# Revit family: Echo Eliminator - Composite Ceiling and Wall Panels
name_source: partatom
category: Specialty Equipment
units: mm (PartAtom-declared; Revit-internal decimal feet)

## family parameters
Always vertical = No
Cut with Voids When Loaded = No
Enable Cutting in Views = Yes
Maintain Annotation Orientation = No
OmniClass Number = 23.35.00.00
OmniClass Title = Covering, Cladding, and Finishes
Part Type = Normal
Room Calculation Point = No
Round Connector Dimension = Use Diameter
Shared = No
Work Plane-Based = Yes

## types (1)
- 4 INCH THICK - 24x48 - Charcoal
    A = 0' - 0"
    Acoustics - NRC = Sound absorption varies from NRC 0.45 to 0.95 based on installation method used when tested per ASTM C423.
    Assembly Code = C30
    Default Elevation = 4' - 0"
    Description = Acoustical Panels
    Finish = Paint - Acoustical-Surfaces - Echo Eliminator - Marble Blue
    Fire Rating = ASTM E84 - Class A
    Length = 4' - 0"
    Manufacturer = Acoustical Surfaces, Inc.
    Material = Echo Eliminator - Composite
    Model = Echo Eliminator - Composite Panels
    Recycled Content Percentage = 0%
    Type Comments = Acoustical Panels
    URL = https://www.acousticalsurfaces.com
    Width = 2' - 0"

## geometry (parser evidence)
native form markers: Sweep x6
no freeform markers — native parametric forms only
